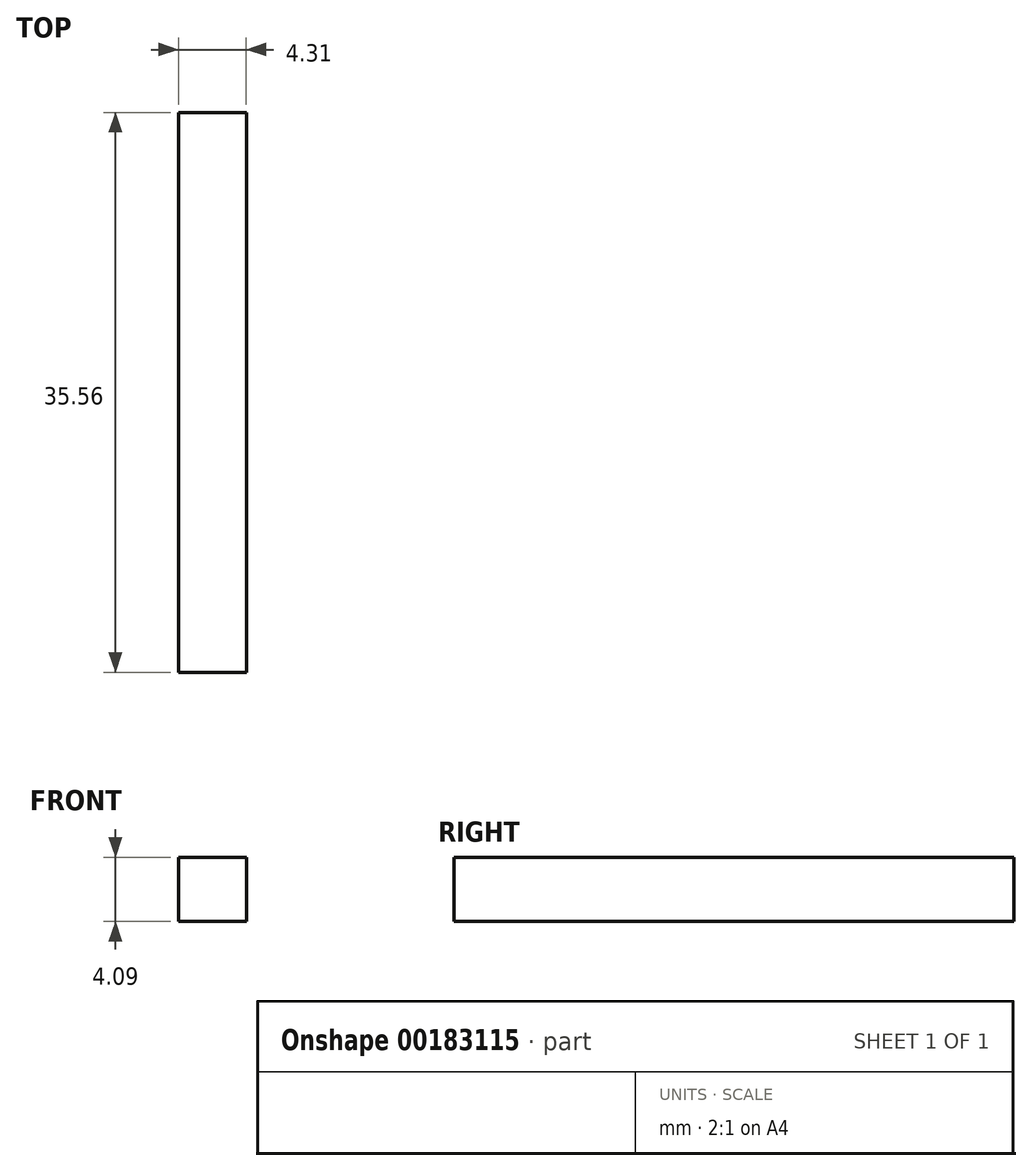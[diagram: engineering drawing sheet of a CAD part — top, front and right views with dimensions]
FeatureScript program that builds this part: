
annotation { "Feature Type Name" : "Feature", "Feature Type Description" : "" }
export const myFeature = defineFeature(function(context is Context, id is Id, definition is map)
    precondition{}
    {
        {
            var Q0;
            Q0=qCreatedBy(makeId("Front.planeOp"),FACE);
            var sketch = newSketch(context, id + "F0", { "sketchPlane" : qUnion([Q0])});
            skLineSegment(sketch, "E0.bottom", {"start": v(-59.13, 34.71) * mm, "end": v(-54.82, 34.71) * mm});
            skLineSegment(sketch, "E0.top", {"start": v(-59.13, 30.62) * mm, "end": v(-54.82, 30.62) * mm});
            skLineSegment(sketch, "E0.left", {"start": v(-59.13, 34.71) * mm, "end": v(-59.13, 30.62) * mm});
            skLineSegment(sketch, "E0.right", {"start": v(-54.82, 34.71) * mm, "end": v(-54.82, 30.62) * mm});
            skSolve(sketch);
        }
        {
            var Q0;
            Q0=makeQuery(id+"F0.imprint","IMPRINT",FACE,{"disambiguationData":[TD([[makeQuery(id+"F0.imprint","IMPRINT",EDGE,{"derivedFrom":sQuery(id+"F0.wireOp",EDGE,"E0.bottom")}),-1.0]])]});
            extrude(context, id + "F1", {"entities" : qUnion([Q0]), "depth" : 35.56 * mm});
        }
    });
